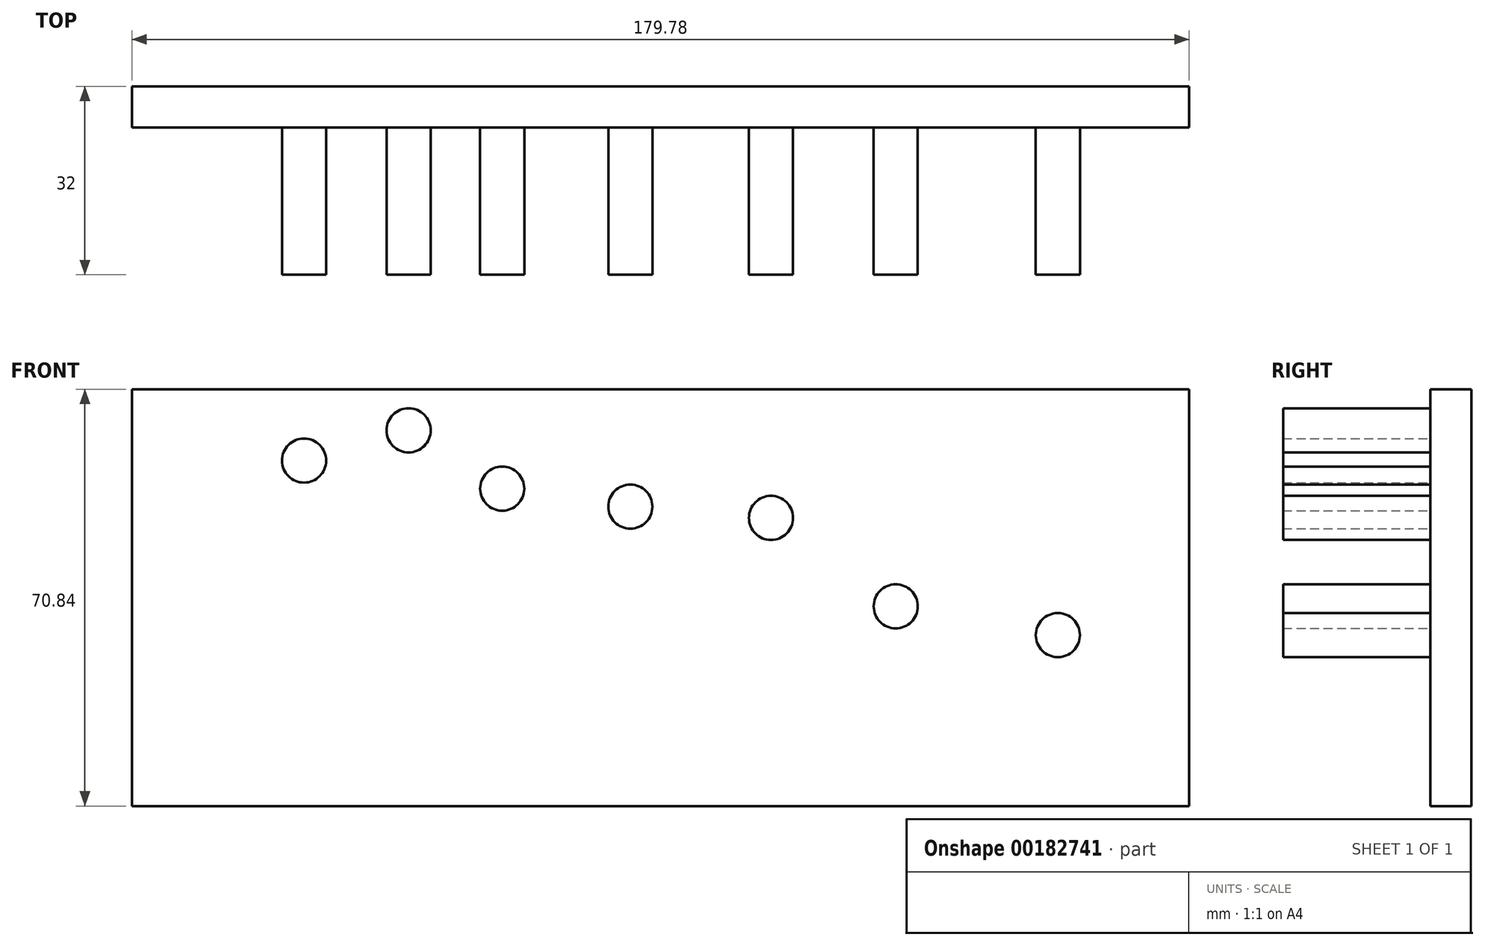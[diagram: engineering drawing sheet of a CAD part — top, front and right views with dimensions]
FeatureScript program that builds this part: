
annotation { "Feature Type Name" : "Feature", "Feature Type Description" : "" }
export const myFeature = defineFeature(function(context is Context, id is Id, definition is map)
    precondition{}
    {
        {
            var Q0;
            Q0=qCreatedBy(makeId("Front.planeOp"),FACE);
            var sketch = newSketch(context, id + "F0", { "sketchPlane" : qUnion([Q0])});
            skLineSegment(sketch, "E0.bottom", {"start": v(-90.98, 58.39) * mm, "end": v(88.8, 58.39) * mm});
            skLineSegment(sketch, "E0.top", {"start": v(-90.98, -12.45) * mm, "end": v(88.8, -12.45) * mm});
            skLineSegment(sketch, "E0.left", {"start": v(-90.98, 58.39) * mm, "end": v(-90.98, -12.45) * mm});
            skLineSegment(sketch, "E0.right", {"start": v(88.8, 58.39) * mm, "end": v(88.8, -12.45) * mm});
            skSolve(sketch);
        }
        {
            var Q0;
            Q0 = qSketchRegion(id + "F0", true);
            extrude(context, id + "F1", {"entities" : qUnion([Q0]), "depth" : 7 * mm});
        }
        {
            var Q0;
            Q0=makeQuery(id+"F1.opExtrude","CAP_FACE",FACE,{"disambiguationData":[OSD([sQuery(id+"F0.wireOp",EDGE,"E0.bottom"),sQuery(id+"F0.wireOp",EDGE,"E0.top"),sQuery(id+"F0.wireOp",EDGE,"E0.left"),sQuery(id+"F0.wireOp",EDGE,"E0.right")])],"isStart":false});
            var sketch = newSketch(context, id + "F2", { "sketchPlane" : qUnion([Q0])});
            skCircle(sketch, "E1", {"center": v(-61.7, 46.28) * mm, "radius": 3.75 * mm});
            skSolve(sketch);
        }
        {
            var Q0;
            Q0 = qSketchRegion(id + "F2", true);
            extrude(context, id + "F3", {"entities" : qUnion([Q0]), "operationType" : NewBodyOperationType.ADD, "depth" : 25 * mm});
        }
        {
            var Q0;
            Q0=makeQuery(id+"F1.opExtrude","CAP_FACE",FACE,{"disambiguationData":[OSD([sQuery(id+"F0.wireOp",EDGE,"E0.bottom"),sQuery(id+"F0.wireOp",EDGE,"E0.top"),sQuery(id+"F0.wireOp",EDGE,"E0.left"),sQuery(id+"F0.wireOp",EDGE,"E0.right")])],"isStart":false});
            var sketch = newSketch(context, id + "F4", { "sketchPlane" : qUnion([Q0])});
            skCircle(sketch, "E2", {"center": v(-43.92, 51.41) * mm, "radius": 3.75 * mm});
            skSolve(sketch);
        }
        {
            var Q0;
            Q0 = qSketchRegion(id + "F4", true);
            extrude(context, id + "F5", {"entities" : qUnion([Q0]), "operationType" : NewBodyOperationType.ADD, "depth" : 25 * mm});
        }
        {
            var Q0;
            Q0=makeQuery(id+"F1.opExtrude","CAP_FACE",FACE,{"disambiguationData":[OSD([sQuery(id+"F0.wireOp",EDGE,"E0.bottom"),sQuery(id+"F0.wireOp",EDGE,"E0.top"),sQuery(id+"F0.wireOp",EDGE,"E0.left"),sQuery(id+"F0.wireOp",EDGE,"E0.right")])],"isStart":false});
            var sketch = newSketch(context, id + "F6", { "sketchPlane" : qUnion([Q0])});
            skCircle(sketch, "E3", {"center": v(-28, 41.5) * mm, "radius": 3.75 * mm});
            skSolve(sketch);
        }
        {
            var Q0;
            Q0 = qSketchRegion(id + "F6", true);
            extrude(context, id + "F7", {"entities" : qUnion([Q0]), "operationType" : NewBodyOperationType.ADD, "depth" : 25 * mm});
        }
        {
            var Q0;
            Q0=makeQuery(id+"F1.opExtrude","CAP_FACE",FACE,{"disambiguationData":[OSD([sQuery(id+"F0.wireOp",EDGE,"E0.bottom"),sQuery(id+"F0.wireOp",EDGE,"E0.top"),sQuery(id+"F0.wireOp",EDGE,"E0.left"),sQuery(id+"F0.wireOp",EDGE,"E0.right")])],"isStart":false});
            var sketch = newSketch(context, id + "F8", { "sketchPlane" : qUnion([Q0])});
            skCircle(sketch, "E4", {"center": v(-6.21, 38.45) * mm, "radius": 3.75 * mm});
            skSolve(sketch);
        }
        {
            var Q0;
            Q0 = qSketchRegion(id + "F8", true);
            extrude(context, id + "F9", {"entities" : qUnion([Q0]), "operationType" : NewBodyOperationType.ADD, "depth" : 25 * mm});
        }
        {
            var Q0;
            Q0=makeQuery(id+"F1.opExtrude","CAP_FACE",FACE,{"disambiguationData":[OSD([sQuery(id+"F0.wireOp",EDGE,"E0.bottom"),sQuery(id+"F0.wireOp",EDGE,"E0.top"),sQuery(id+"F0.wireOp",EDGE,"E0.left"),sQuery(id+"F0.wireOp",EDGE,"E0.right")])],"isStart":false});
            var sketch = newSketch(context, id + "F10", { "sketchPlane" : qUnion([Q0])});
            skCircle(sketch, "E5", {"center": v(17.71, 36.53) * mm, "radius": 3.75 * mm});
            skSolve(sketch);
        }
        {
            var Q0;
            Q0 = qSketchRegion(id + "F10", true);
            extrude(context, id + "F11", {"entities" : qUnion([Q0]), "operationType" : NewBodyOperationType.ADD, "depth" : 25 * mm});
        }
        {
            var Q0;
            Q0=makeQuery(id+"F1.opExtrude","CAP_FACE",FACE,{"disambiguationData":[OSD([sQuery(id+"F0.wireOp",EDGE,"E0.bottom"),sQuery(id+"F0.wireOp",EDGE,"E0.top"),sQuery(id+"F0.wireOp",EDGE,"E0.left"),sQuery(id+"F0.wireOp",EDGE,"E0.right")])],"isStart":false});
            var sketch = newSketch(context, id + "F12", { "sketchPlane" : qUnion([Q0])});
            skCircle(sketch, "E6", {"center": v(38.92, 21.5) * mm, "radius": 3.75 * mm});
            skSolve(sketch);
        }
        {
            var Q0;
            Q0 = qSketchRegion(id + "F12", true);
            extrude(context, id + "F13", {"entities" : qUnion([Q0]), "operationType" : NewBodyOperationType.ADD, "depth" : 25 * mm});
        }
        {
            var Q0;
            Q0=makeQuery(id+"F1.opExtrude","CAP_FACE",FACE,{"disambiguationData":[OSD([sQuery(id+"F0.wireOp",EDGE,"E0.bottom"),sQuery(id+"F0.wireOp",EDGE,"E0.top"),sQuery(id+"F0.wireOp",EDGE,"E0.left"),sQuery(id+"F0.wireOp",EDGE,"E0.right")])],"isStart":false});
            var sketch = newSketch(context, id + "F14", { "sketchPlane" : qUnion([Q0])});
            skCircle(sketch, "E7", {"center": v(66.5, 16.6) * mm, "radius": 3.75 * mm});
            skSolve(sketch);
        }
        {
            var Q0;
            Q0 = qSketchRegion(id + "F14", true);
            extrude(context, id + "F15", {"entities" : qUnion([Q0]), "operationType" : NewBodyOperationType.ADD, "depth" : 25 * mm});
        }
    });
